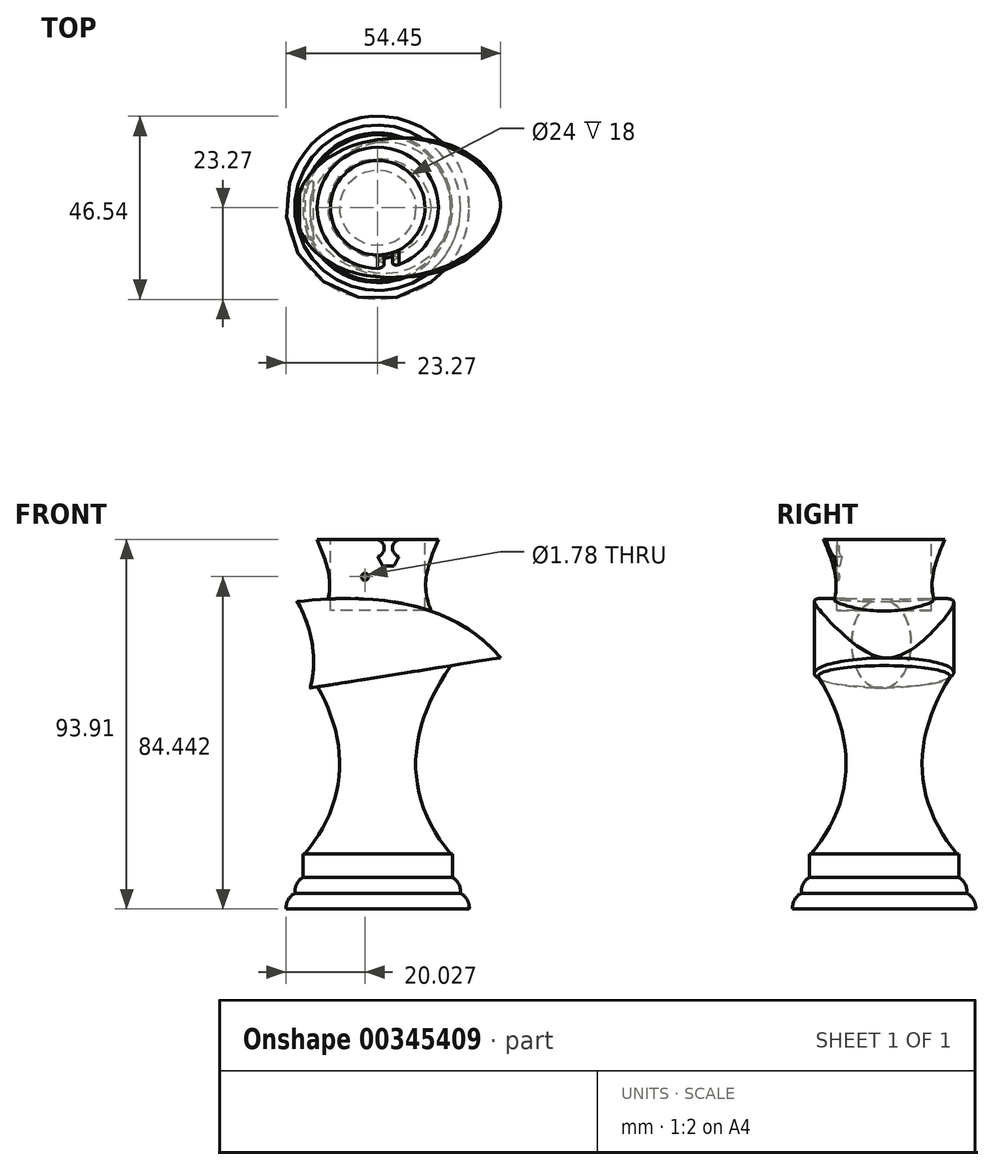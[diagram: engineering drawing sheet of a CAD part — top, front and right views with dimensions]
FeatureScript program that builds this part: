
annotation { "Feature Type Name" : "Feature", "Feature Type Description" : "" }
export const myFeature = defineFeature(function(context is Context, id is Id, definition is map)
    precondition{}
    {
        {
            var Q0;
            Q0=qCreatedBy(makeId("Front.planeOp"),FACE);
            var sketch = newSketch(context, id + "F0", { "sketchPlane" : qUnion([Q0])});
            skLineSegment(sketch, "E0", {"start": v(0, 32.1) * mm, "end": v(0, -20.1) * mm, "construction": true});
            skLineSegment(sketch, "E1.bottom", {"start": v(0, 6) * mm, "end": v(19, 6) * mm});
            skLineSegment(sketch, "E1.left", {"start": v(0, 6) * mm, "end": v(0, 0) * mm});
            skLineSegment(sketch, "E1.right", {"start": v(19, 6) * mm, "end": v(19, 0) * mm});
            skLineSegment(sketch, "E2.MirrorCS", {"start": v(0, -32.1) * mm, "end": v(0, 20.1) * mm, "construction": true});
            skLineSegment(sketch, "E3", {"start": v(19, 0) * mm, "end": v(0, 0) * mm});
            skSolve(sketch);
        }
        {
            var Q0;
            Q0 = qSketchRegion(id + "F0", true);
            var Q1;
            Q1=sQuery(id+"F0.wireOp",EDGE,"E2.MirrorCS");
            revolve(context, id + "F1", {"entities" : qUnion([Q0]), "axis" : qUnion([Q1]), "revolveType" : RevolveType.FULL});
        }
        {
            var Q0;
            Q0=qCreatedBy(makeId("Front.planeOp"),FACE);
            var sketch = newSketch(context, id + "F2", { "sketchPlane" : qUnion([Q0])});
            skLineSegment(sketch, "E4", {"start": v(0, 57.22) * mm, "end": v(0, -6.91) * mm, "construction": true});
            skLineSegment(sketch, "E5", {"start": v(0, 5.86) * mm, "end": v(18.65, 5.86) * mm});
            skLineSegment(sketch, "E6", {"start": v(0, 5.86) * mm, "end": v(0, 53.86) * mm});
            skFitSpline(sketch, "E7", {"points": [v(18.65, 5.86) * mm, v(18.65, 53.86) * mm], "startDerivative": vector(-35.72, 42.6) * mm, "endDerivative": vector(36.3, 51.52) * mm});
            skLineSegment(sketch, "E8", {"start": v(18.65, 53.86) * mm, "end": v(0, 53.86) * mm});
            skSolve(sketch);
        }
        {
            var Q0;
            Q0 = qSketchRegion(id + "F2", true);
            var Q1;
            Q1=sQuery(id+"F2.wireOp",EDGE,"E4");
            revolve(context, id + "F3", {"operationType" : NewBodyOperationType.ADD, "entities" : qUnion([Q0]), "axis" : qUnion([Q1]), "revolveType" : RevolveType.FULL});
        }
        {
            var Q0;
            Q0=qCreatedBy(makeId("Front.planeOp"),FACE);
            var sketch = newSketch(context, id + "F4", { "sketchPlane" : qUnion([Q0])});
            skLineSegment(sketch, "E9", {"start": v(-18.25, 47.97) * mm, "end": v(22.08, 54.4) * mm});
            skLineSegment(sketch, "E10", {"start": v(22.08, 54.4) * mm, "end": v(2.8, 83.8) * mm});
            skLineSegment(sketch, "E11", {"start": v(2.8, 83.8) * mm, "end": v(-19.2, 83.8) * mm});
            skLineSegment(sketch, "E12", {"start": v(-19.2, 83.8) * mm, "end": v(-28.37, 83.8) * mm});
            skLineSegment(sketch, "E13", {"start": v(-28.37, 83.8) * mm, "end": v(-28.37, 50.84) * mm});
            skLineSegment(sketch, "E14", {"start": v(-28.37, 50.84) * mm, "end": v(-18.25, 47.97) * mm});
            skSolve(sketch);
        }
        {
            var Q0;
            Q0 = qSketchRegion(id + "F4", true);
            extrude(context, id + "F5", {"entities" : qUnion([Q0]), "operationType" : NewBodyOperationType.REMOVE, "endBound" : BoundingType.SYMMETRIC, "oppositeDirection" : true, "depth" : 39.6 * mm});
        }
        {
            var Q0;
            Q0=makeQuery(id+"F5.boolean.opBoolean","COPY",FACE,{"derivedFrom":makeQuery(id+"F5.opExtrude","SWEPT_FACE",FACE,{"disambiguationData":[OSD([sQuery(id+"F4.wireOp",EDGE,"E9")])]})});
            var sketch = newSketch(context, id + "F6", { "sketchPlane" : qUnion([Q0])});
            skEllipse(sketch, "E15", {"center": v(15.1, 0) * mm, "majorRadius": 24.52 * mm, "minorRadius": 17.67 * mm, "majorAxis": v(1, 0.07)});
            skSolve(sketch);
        }
        {
            var Q0;
            Q0 = qSketchRegion(id + "F6", true);
            extrude(context, id + "F7", {"entities" : qUnion([Q0]), "operationType" : NewBodyOperationType.ADD, "depth" : 22.2 * mm});
        }
        {
            var Q0;
            Q0=qCreatedBy(makeId("Front.planeOp"),FACE);
            var sketch = newSketch(context, id + "F8", { "sketchPlane" : qUnion([Q0])});
            skFitSpline(sketch, "E16", {"points": [v(31.2, 55.84) * mm, v(-20.5, 70.13) * mm], "startDerivative": vector(-36, 42.5) * mm, "endDerivative": vector(-61.5, -7) * mm});
            skFitSpline(sketch, "E17", {"points": [v(-20.5, 70.13) * mm, v(-17.15, 48.03) * mm], "startDerivative": vector(12.7, -21.4) * mm, "endDerivative": vector(-5.32, -21.27) * mm});
            skLineSegment(sketch, "E18", {"start": v(31.2, 55.84) * mm, "end": v(38.97, 82.3) * mm});
            skLineSegment(sketch, "E19", {"start": v(38.97, 82.3) * mm, "end": v(19.48, 85.25) * mm});
            skLineSegment(sketch, "E20", {"start": v(19.48, 85.25) * mm, "end": v(-16.76, 80.22) * mm});
            skLineSegment(sketch, "E21", {"start": v(-16.76, 80.22) * mm, "end": v(-32.31, 69.5) * mm});
            skLineSegment(sketch, "E22", {"start": v(-32.31, 69.5) * mm, "end": v(-25.62, 46.35) * mm});
            skLineSegment(sketch, "E23", {"start": v(-25.62, 46.35) * mm, "end": v(-17.15, 48.03) * mm});
            skSolve(sketch);
        }
        {
            var Q0;
            Q0 = qSketchRegion(id + "F8", true);
            extrude(context, id + "F9", {"entities" : qUnion([Q0]), "operationType" : NewBodyOperationType.REMOVE, "endBound" : BoundingType.SYMMETRIC, "depth" : 58 * mm});
        }
        {
            var Q0;
            Q0=makeQuery(id+"F9.boolean.opBoolean","COPY",FACE,{"derivedFrom":makeQuery(id+"F9.opExtrude","SWEPT_FACE",FACE,{"disambiguationData":[OSD([sQuery(id+"F8.wireOp",EDGE,"E17")])]})});
            fillet(context, id + "F10", {"entities" : qUnion([Q0]), "radius" : 0.01 * mm, "tangentPropagation" : true, "allowEdgeOverflow" : false});
        }
        {
            var Q0;
            Q0=qCreatedBy(makeId("Front.planeOp"),FACE);
            var sketch = newSketch(context, id + "F11", { "sketchPlane" : qUnion([Q0])});
            skLineSegment(sketch, "E24", {"start": v(0, 60.1) * mm, "end": v(0, 124.28) * mm, "construction": true});
            skLineSegment(sketch, "E25", {"start": v(0, 63.57) * mm, "end": v(15.4, 63.57) * mm});
            skFitSpline(sketch, "E26", {"points": [v(15.4, 63.57) * mm, v(15.4, 85.91) * mm], "startDerivative": vector(-14.49, 28.28) * mm, "endDerivative": vector(11.04, 26.21) * mm});
            skLineSegment(sketch, "E27", {"start": v(15.4, 85.91) * mm, "end": v(0, 85.91) * mm});
            skLineSegment(sketch, "E28", {"start": v(0, 85.91) * mm, "end": v(0, 63.57) * mm});
            skSolve(sketch);
        }
        {
            var Q0;
            Q0 = qSketchRegion(id + "F11", true);
            var Q1;
            Q1=sQuery(id+"F11.wireOp",EDGE,"E24");
            revolve(context, id + "F12", {"operationType" : NewBodyOperationType.ADD, "entities" : qUnion([Q0]), "axis" : qUnion([Q1]), "revolveType" : RevolveType.FULL});
        }
        {
            var Q0;
            Q0=makeQuery(id+"F12.opRevolve","SWEPT_FACE",FACE,{"disambiguationData":[OSD([sQuery(id+"F11.wireOp",EDGE,"E27")])]});
            var sketch = newSketch(context, id + "F13", { "sketchPlane" : qUnion([Q0])});
            skCircle(sketch, "E29", {"center": v(0, 0) * mm, "radius": 12 * mm});
            skSolve(sketch);
        }
        {
            var Q0;
            Q0=makeQuery(id+"F13.imprint","IMPRINT",FACE,{"disambiguationData":[TD([[makeQuery(id+"F13.imprint","IMPRINT",EDGE,{"derivedFrom":sQuery(id+"F13.wireOp",EDGE,"E29")}),1.0]])]});
            extrude(context, id + "F14", {"entities" : qUnion([Q0]), "operationType" : NewBodyOperationType.REMOVE, "endBound" : BoundingType.SYMMETRIC, "oppositeDirection" : true, "depth" : 36 * mm});
        }
        {
            var Q0;
            Q0=qCreatedBy(makeId("Front.planeOp"),FACE);
            var sketch = newSketch(context, id + "F15", { "sketchPlane" : qUnion([Q0])});
            skArc(sketch, "E30", {"start": v(0, 81.54) * mm, "mid": v(1.64, 83.72) * mm, "end": v(0, 85.91) * mm});
            skLineSegment(sketch, "E31", {"start": v(1.26, 79.18) * mm, "end": v(2.7, 79.18) * mm});
            skLineSegment(sketch, "E32", {"start": v(2.7, 79.18) * mm, "end": v(2.7, 92.86) * mm, "construction": true});
            skLineSegment(sketch, "E33", {"start": v(0, 81.54) * mm, "end": v(1.26, 79.18) * mm});
            skArc(sketch, "E34.MirrorCS", {"start": v(5.4, 81.54) * mm, "mid": v(3.76, 83.72) * mm, "end": v(5.4, 85.91) * mm});
            skLineSegment(sketch, "E35.MirrorCS", {"start": v(5.4, 81.54) * mm, "end": v(4.14, 79.18) * mm});
            skLineSegment(sketch, "E36.MirrorCS", {"start": v(4.14, 79.18) * mm, "end": v(2.7, 79.18) * mm});
            skLineSegment(sketch, "E37", {"start": v(0, 85.91) * mm, "end": v(5.4, 85.91) * mm});
            skSolve(sketch);
        }
        {
            var Q0;
            Q0 = qSketchRegion(id + "F15", true);
            extrude(context, id + "F16", {"entities" : qUnion([Q0]), "operationType" : NewBodyOperationType.REMOVE, "depth" : 20.8 * mm});
        }
        {
            var Q0;
            Q0=qCreatedBy(makeId("Front.planeOp"),FACE);
            var sketch = newSketch(context, id + "F17", { "sketchPlane" : qUnion([Q0])});
            skCircle(sketch, "E38", {"center": v(-3.24, 76.44) * mm, "radius": 0.9 * mm});
            skSolve(sketch);
        }
        {
            var Q0;
            Q0 = qSketchRegion(id + "F17", true);
            extrude(context, id + "F18", {"entities" : qUnion([Q0]), "operationType" : NewBodyOperationType.REMOVE, "depth" : 15.1 * mm});
        }
        {
            var Q0;
            Q0=qCreatedBy(makeId("Front.planeOp"),FACE);
            var sketch = newSketch(context, id + "F19", { "sketchPlane" : qUnion([Q0])});
            skLineSegment(sketch, "E39", {"start": v(0, 0) * mm, "end": v(0, -4) * mm});
            skLineSegment(sketch, "E40", {"start": v(0, 0) * mm, "end": v(19, 0) * mm});
            skLineSegment(sketch, "E41", {"start": v(0, -4) * mm, "end": v(21, -4) * mm});
            skArc(sketch, "E42", {"start": v(21, -4) * mm, "mid": v(20.61, -1.7) * mm, "end": v(19, 0) * mm});
            skLineSegment(sketch, "E43", {"start": v(0, -4) * mm, "end": v(0, -8) * mm});
            skLineSegment(sketch, "E44", {"start": v(0, -8) * mm, "end": v(23.25, -8) * mm});
            skArc(sketch, "E45", {"start": v(23.25, -8) * mm, "mid": v(22.76, -5.64) * mm, "end": v(21, -4) * mm});
            skLineSegment(sketch, "E46", {"start": v(0, 6.07) * mm, "end": v(0, -17.15) * mm, "construction": true});
            skSolve(sketch);
        }
        {
            var Q0;
            Q0 = qSketchRegion(id + "F19", true);
            var Q1;
            Q1=sQuery(id+"F19.wireOp",EDGE,"E46");
            revolve(context, id + "F20", {"operationType" : NewBodyOperationType.ADD, "entities" : qUnion([Q0]), "axis" : qUnion([Q1]), "revolveType" : RevolveType.FULL});
        }
    });
